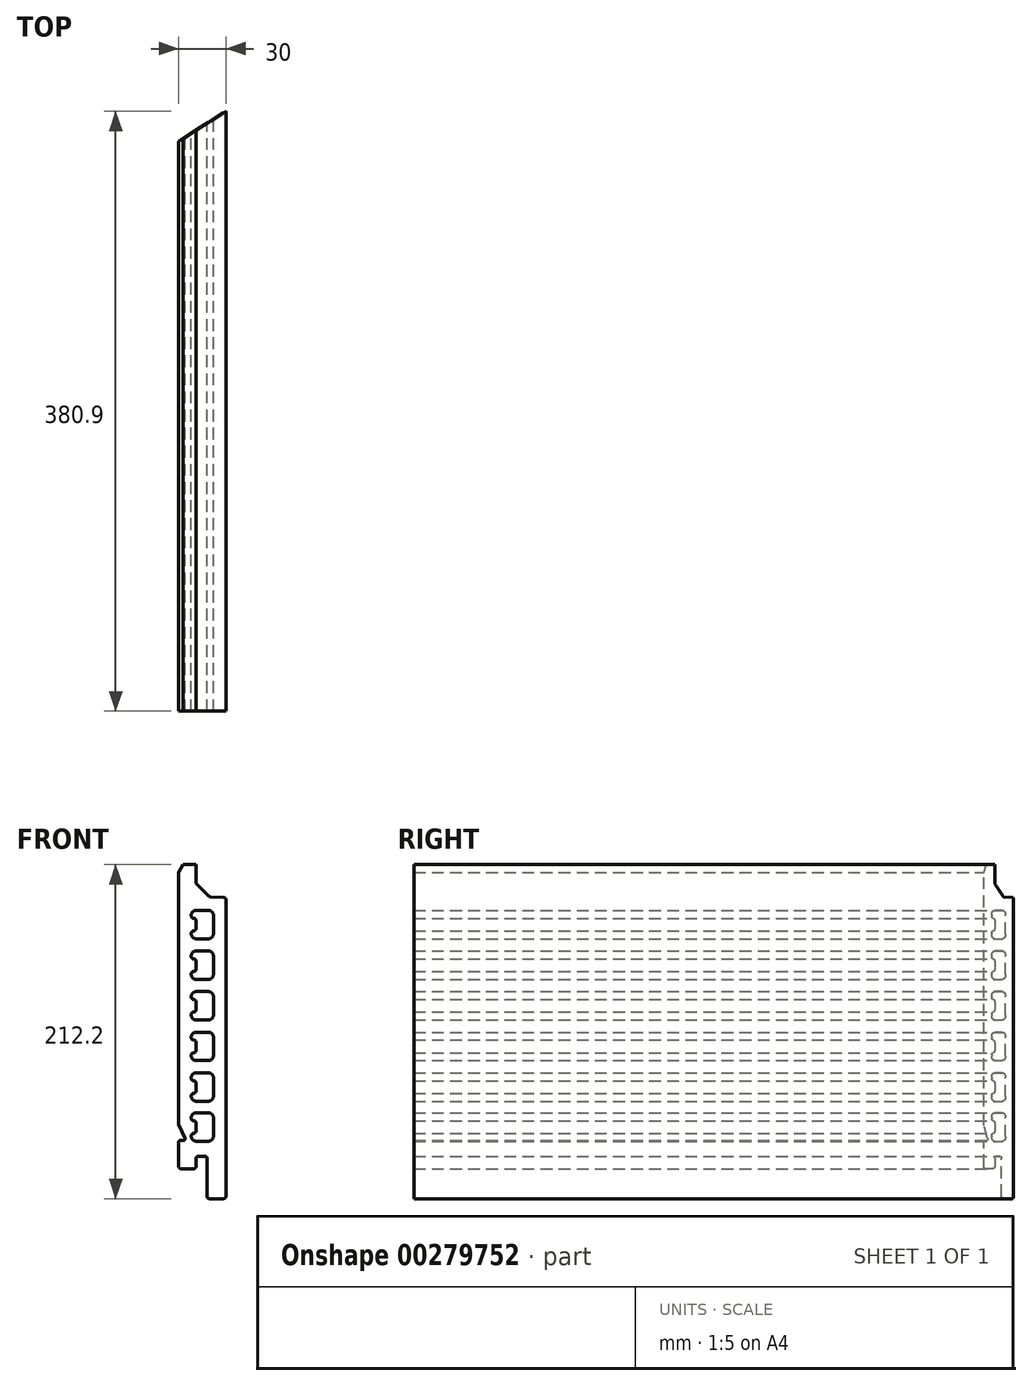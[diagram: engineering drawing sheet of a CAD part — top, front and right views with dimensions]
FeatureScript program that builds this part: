
annotation { "Feature Type Name" : "Feature", "Feature Type Description" : "" }
export const myFeature = defineFeature(function(context is Context, id is Id, definition is map)
    precondition{}
    {
        {
            var Q0;
            Q0=qCreatedBy(makeId("Front.planeOp"),FACE);
            var sketch = newSketch(context, id + "F0", { "sketchPlane" : qUnion([Q0])});
            skLineSegment(sketch, "E0", {"start": v(-14.86, -59.63) * mm, "end": v(-11.1, -67.7) * mm});
            skArc(sketch, "E1", {"start": v(-11.1, -67.7) * mm, "mid": v(-11.16, -68.66) * mm, "end": v(-12, -69.12) * mm});
            skLineSegment(sketch, "E2", {"start": v(-12, -69.12) * mm, "end": v(-14, -69.12) * mm});
            skArc(sketch, "E3", {"start": v(-14, -69.12) * mm, "mid": v(-14.7, -69.41) * mm, "end": v(-15, -70.12) * mm});
            skLineSegment(sketch, "E4", {"start": v(-15, -70.12) * mm, "end": v(-15, -85.6) * mm});
            skArc(sketch, "E5", {"start": v(-15, -85.6) * mm, "mid": v(-14.56, -86.66) * mm, "end": v(-13.5, -87.1) * mm});
            skLineSegment(sketch, "E6", {"start": v(-13.5, -87.1) * mm, "end": v(-5.5, -87.1) * mm});
            skArc(sketch, "E7", {"start": v(-5.5, -87.1) * mm, "mid": v(-4.44, -86.66) * mm, "end": v(-4, -85.6) * mm});
            skLineSegment(sketch, "E8", {"start": v(-4, -85.6) * mm, "end": v(-4, -80.6) * mm});
            skArc(sketch, "E9", {"start": v(-4, -80.6) * mm, "mid": v(-3.56, -79.54) * mm, "end": v(-2.5, -79.1) * mm});
            skLineSegment(sketch, "E10", {"start": v(-2.5, -79.1) * mm, "end": v(1.48, -79.1) * mm});
            skArc(sketch, "E11", {"start": v(1.48, -79.1) * mm, "mid": v(2.54, -79.54) * mm, "end": v(2.98, -80.6) * mm});
            skLineSegment(sketch, "E12", {"start": v(2.98, -80.6) * mm, "end": v(2.98, -104.6) * mm});
            skArc(sketch, "E13", {"start": v(2.98, -104.6) * mm, "mid": v(3.42, -105.66) * mm, "end": v(4.48, -106.1) * mm});
            skLineSegment(sketch, "E14", {"start": v(4.48, -106.1) * mm, "end": v(13.5, -106.1) * mm});
            skArc(sketch, "E15", {"start": v(13.5, -106.1) * mm, "mid": v(14.56, -105.66) * mm, "end": v(15, -104.6) * mm});
            skLineSegment(sketch, "E16", {"start": v(15, -104.6) * mm, "end": v(15, 83.78) * mm});
            skArc(sketch, "E17", {"start": v(15, 83.78) * mm, "mid": v(14.58, 84.81) * mm, "end": v(13.57, 85.27) * mm});
            skLineSegment(sketch, "E18", {"start": v(13.57, 85.27) * mm, "end": v(5.1, 85.66) * mm});
            skArc(sketch, "E19", {"start": v(5.1, 85.66) * mm, "mid": v(4.57, 85.79) * mm, "end": v(4.11, 86.1) * mm});
            skLineSegment(sketch, "E20", {"start": v(4.11, 86.1) * mm, "end": v(-3.56, 93.77) * mm});
            skArc(sketch, "E21", {"start": v(-3.56, 93.77) * mm, "mid": v(-3.89, 94.26) * mm, "end": v(-4, 94.83) * mm});
            skLineSegment(sketch, "E22", {"start": v(-4, 94.83) * mm, "end": v(-4, 106.1) * mm});
            skLineSegment(sketch, "E23", {"start": v(-4, 106.1) * mm, "end": v(-12.31, 106.1) * mm});
            skLineSegment(sketch, "E24", {"start": v(-12.31, 106.1) * mm, "end": v(-15, 101.2) * mm});
            skLineSegment(sketch, "E25", {"start": v(-15, 101.2) * mm, "end": v(-15, -59) * mm});
            skArc(sketch, "E26", {"start": v(-15, -59) * mm, "mid": v(-14.96, -59.32) * mm, "end": v(-14.86, -59.63) * mm});
            skArc(sketch, "E27", {"start": v(-14.86, -59.63) * mm, "mid": v(-14.96, -59.32) * mm, "end": v(-15, -59) * mm});
            skSolve(sketch);
        }
        {
            var Q0;
            Q0=makeQuery(id+"F0.imprint","IMPRINT",FACE,{"disambiguationData":[TD([[makeQuery(id+"F0.imprint","IMPRINT",EDGE,{"derivedFrom":sQuery(id+"F0.wireOp",EDGE,"E3")}),1.0]])]});
            extrude(context, id + "F1", {"entities" : qUnion([Q0]), "depth" : 381 * mm});
        }
        {
            var Q0;
            Q0=qCreatedBy(makeId("Front.planeOp"),FACE);
            var sketch = newSketch(context, id + "F2", { "sketchPlane" : qUnion([Q0])});
            skArc(sketch, "E28", {"start": v(-4, -32.7) * mm, "mid": v(-4.43, -31.63) * mm, "end": v(-5.5, -31.2) * mm});
            skLineSegment(sketch, "E29", {"start": v(-5.5, -31.2) * mm, "end": v(-5.5, -31.2) * mm});
            skArc(sketch, "E30", {"start": v(-5.5, -31.2) * mm, "mid": v(-6.56, -30.76) * mm, "end": v(-7, -29.7) * mm});
            skLineSegment(sketch, "E31", {"start": v(-7, -29.7) * mm, "end": v(-7, -29.2) * mm});
            skArc(sketch, "E32", {"start": v(-7, -29.2) * mm, "mid": v(-6.12, -27.07) * mm, "end": v(-4, -26.2) * mm});
            skLineSegment(sketch, "E33", {"start": v(-4, -26.2) * mm, "end": v(4, -26.2) * mm});
            skArc(sketch, "E34", {"start": v(4, -26.2) * mm, "mid": v(6.12, -27.07) * mm, "end": v(7, -29.2) * mm});
            skLineSegment(sketch, "E35", {"start": v(7, -29.2) * mm, "end": v(7, -41.2) * mm});
            skArc(sketch, "E36", {"start": v(7, -41.2) * mm, "mid": v(6.12, -43.32) * mm, "end": v(4, -44.2) * mm});
            skLineSegment(sketch, "E37", {"start": v(4, -44.2) * mm, "end": v(-4, -44.2) * mm});
            skArc(sketch, "E38", {"start": v(-4, -44.2) * mm, "mid": v(-6.12, -43.32) * mm, "end": v(-7, -41.2) * mm});
            skLineSegment(sketch, "E39", {"start": v(-7, -41.2) * mm, "end": v(-7, -40.7) * mm});
            skArc(sketch, "E40", {"start": v(-7, -40.7) * mm, "mid": v(-6.56, -39.63) * mm, "end": v(-5.5, -39.2) * mm});
            skLineSegment(sketch, "E41", {"start": v(-5.5, -39.2) * mm, "end": v(-5.5, -39.2) * mm});
            skArc(sketch, "E42", {"start": v(-5.5, -39.2) * mm, "mid": v(-4.43, -38.76) * mm, "end": v(-4, -37.7) * mm});
            skLineSegment(sketch, "E43", {"start": v(-4, -37.7) * mm, "end": v(-4, -32.7) * mm});
            skArc(sketch, "E44", {"start": v(-4, -58.1) * mm, "mid": v(-4.43, -57.03) * mm, "end": v(-5.5, -56.6) * mm});
            skLineSegment(sketch, "E45", {"start": v(-5.5, -56.6) * mm, "end": v(-5.5, -56.6) * mm});
            skArc(sketch, "E46", {"start": v(-5.5, -56.6) * mm, "mid": v(-6.56, -56.16) * mm, "end": v(-7, -55.1) * mm});
            skLineSegment(sketch, "E47", {"start": v(-7, -55.1) * mm, "end": v(-7, -54.6) * mm});
            skArc(sketch, "E48", {"start": v(-7, -54.6) * mm, "mid": v(-6.12, -52.47) * mm, "end": v(-4, -51.6) * mm});
            skLineSegment(sketch, "E49", {"start": v(-4, -51.6) * mm, "end": v(4, -51.6) * mm});
            skArc(sketch, "E50", {"start": v(4, -51.6) * mm, "mid": v(6.12, -52.47) * mm, "end": v(7, -54.6) * mm});
            skLineSegment(sketch, "E51", {"start": v(7, -54.6) * mm, "end": v(7, -66.6) * mm});
            skArc(sketch, "E52", {"start": v(7, -66.6) * mm, "mid": v(6.12, -68.72) * mm, "end": v(4, -69.6) * mm});
            skLineSegment(sketch, "E53", {"start": v(4, -69.6) * mm, "end": v(-4, -69.6) * mm});
            skArc(sketch, "E54", {"start": v(-4, -69.6) * mm, "mid": v(-6.12, -68.72) * mm, "end": v(-7, -66.6) * mm});
            skLineSegment(sketch, "E55", {"start": v(-7, -66.6) * mm, "end": v(-7, -66.1) * mm});
            skArc(sketch, "E56", {"start": v(-7, -66.1) * mm, "mid": v(-6.56, -65.03) * mm, "end": v(-5.5, -64.6) * mm});
            skLineSegment(sketch, "E57", {"start": v(-5.5, -64.6) * mm, "end": v(-5.5, -64.6) * mm});
            skArc(sketch, "E58", {"start": v(-5.5, -64.6) * mm, "mid": v(-4.43, -64.16) * mm, "end": v(-4, -63.1) * mm});
            skLineSegment(sketch, "E59", {"start": v(-4, -63.1) * mm, "end": v(-4, -58.1) * mm});
            skArc(sketch, "E60", {"start": v(-4, -6.9) * mm, "mid": v(-4.43, -5.83) * mm, "end": v(-5.5, -5.4) * mm});
            skLineSegment(sketch, "E61", {"start": v(-5.5, -5.4) * mm, "end": v(-5.5, -5.4) * mm});
            skArc(sketch, "E62", {"start": v(-5.5, -5.4) * mm, "mid": v(-6.56, -4.96) * mm, "end": v(-7, -3.9) * mm});
            skLineSegment(sketch, "E63", {"start": v(-7, -3.9) * mm, "end": v(-7, -3.4) * mm});
            skArc(sketch, "E64", {"start": v(-7, -3.4) * mm, "mid": v(-6.12, -1.27) * mm, "end": v(-4, -0.4) * mm});
            skLineSegment(sketch, "E65", {"start": v(-4, -0.4) * mm, "end": v(4, -0.4) * mm});
            skArc(sketch, "E66", {"start": v(4, -0.4) * mm, "mid": v(6.12, -1.27) * mm, "end": v(7, -3.4) * mm});
            skLineSegment(sketch, "E67", {"start": v(7, -3.4) * mm, "end": v(7, -15.4) * mm});
            skArc(sketch, "E68", {"start": v(7, -15.4) * mm, "mid": v(6.12, -17.52) * mm, "end": v(4, -18.4) * mm});
            skLineSegment(sketch, "E69", {"start": v(4, -18.4) * mm, "end": v(-4, -18.4) * mm});
            skArc(sketch, "E70", {"start": v(-4, -18.4) * mm, "mid": v(-6.12, -17.52) * mm, "end": v(-7, -15.4) * mm});
            skLineSegment(sketch, "E71", {"start": v(-7, -15.4) * mm, "end": v(-7, -14.9) * mm});
            skArc(sketch, "E72", {"start": v(-7, -14.9) * mm, "mid": v(-6.56, -13.83) * mm, "end": v(-5.5, -13.4) * mm});
            skLineSegment(sketch, "E73", {"start": v(-5.5, -13.4) * mm, "end": v(-5.5, -13.4) * mm});
            skArc(sketch, "E74", {"start": v(-5.5, -13.4) * mm, "mid": v(-4.43, -12.96) * mm, "end": v(-4, -11.9) * mm});
            skLineSegment(sketch, "E75", {"start": v(-4, -11.9) * mm, "end": v(-4, -6.9) * mm});
            skLineSegment(sketch, "E76", {"start": v(-5.5, 20.4) * mm, "end": v(-5.5, 20.4) * mm});
            skArc(sketch, "E77", {"start": v(-5.5, 20.4) * mm, "mid": v(-6.56, 20.84) * mm, "end": v(-7, 21.9) * mm});
            skLineSegment(sketch, "E78", {"start": v(-7, 21.9) * mm, "end": v(-7, 22.4) * mm});
            skArc(sketch, "E79", {"start": v(-7, 22.4) * mm, "mid": v(-6.12, 24.52) * mm, "end": v(-4, 25.4) * mm});
            skLineSegment(sketch, "E80", {"start": v(-4, 25.4) * mm, "end": v(4, 25.4) * mm});
            skArc(sketch, "E81", {"start": v(4, 25.4) * mm, "mid": v(6.12, 24.52) * mm, "end": v(7, 22.4) * mm});
            skLineSegment(sketch, "E82", {"start": v(7, 22.4) * mm, "end": v(7, 10.4) * mm});
            skArc(sketch, "E83", {"start": v(7, 10.4) * mm, "mid": v(6.12, 8.28) * mm, "end": v(4, 7.4) * mm});
            skLineSegment(sketch, "E84", {"start": v(4, 7.4) * mm, "end": v(-4, 7.4) * mm});
            skArc(sketch, "E85", {"start": v(-4, 7.4) * mm, "mid": v(-6.12, 8.28) * mm, "end": v(-7, 10.4) * mm});
            skLineSegment(sketch, "E86", {"start": v(-7, 10.4) * mm, "end": v(-7, 10.9) * mm});
            skArc(sketch, "E87", {"start": v(-7, 10.9) * mm, "mid": v(-6.56, 11.96) * mm, "end": v(-5.5, 12.4) * mm});
            skLineSegment(sketch, "E88", {"start": v(-5.5, 12.4) * mm, "end": v(-5.5, 12.4) * mm});
            skArc(sketch, "E89", {"start": v(-5.5, 12.4) * mm, "mid": v(-4.43, 12.84) * mm, "end": v(-4, 13.9) * mm});
            skLineSegment(sketch, "E90", {"start": v(-4, 13.9) * mm, "end": v(-4, 18.9) * mm});
            skArc(sketch, "E91", {"start": v(-4, 18.9) * mm, "mid": v(-4.43, 19.96) * mm, "end": v(-5.5, 20.4) * mm});
            skLineSegment(sketch, "E92", {"start": v(-5.5, 46.2) * mm, "end": v(-5.5, 46.2) * mm});
            skArc(sketch, "E93", {"start": v(-5.5, 46.2) * mm, "mid": v(-6.56, 46.64) * mm, "end": v(-7, 47.7) * mm});
            skLineSegment(sketch, "E94", {"start": v(-7, 47.7) * mm, "end": v(-7, 48.2) * mm});
            skArc(sketch, "E95", {"start": v(-7, 48.2) * mm, "mid": v(-6.12, 50.32) * mm, "end": v(-4, 51.2) * mm});
            skLineSegment(sketch, "E96", {"start": v(-4, 51.2) * mm, "end": v(4, 51.2) * mm});
            skArc(sketch, "E97", {"start": v(4, 51.2) * mm, "mid": v(6.12, 50.32) * mm, "end": v(7, 48.2) * mm});
            skLineSegment(sketch, "E98", {"start": v(7, 48.2) * mm, "end": v(7, 36.2) * mm});
            skArc(sketch, "E99", {"start": v(7, 36.2) * mm, "mid": v(6.12, 34.08) * mm, "end": v(4, 33.2) * mm});
            skLineSegment(sketch, "E100", {"start": v(4, 33.2) * mm, "end": v(-4, 33.2) * mm});
            skArc(sketch, "E101", {"start": v(-4, 33.2) * mm, "mid": v(-6.12, 34.08) * mm, "end": v(-7, 36.2) * mm});
            skLineSegment(sketch, "E102", {"start": v(-7, 36.2) * mm, "end": v(-7, 36.7) * mm});
            skArc(sketch, "E103", {"start": v(-7, 36.7) * mm, "mid": v(-6.56, 37.76) * mm, "end": v(-5.5, 38.2) * mm});
            skLineSegment(sketch, "E104", {"start": v(-5.5, 38.2) * mm, "end": v(-5.5, 38.2) * mm});
            skArc(sketch, "E105", {"start": v(-5.5, 38.2) * mm, "mid": v(-4.43, 38.64) * mm, "end": v(-4, 39.7) * mm});
            skLineSegment(sketch, "E106", {"start": v(-4, 39.7) * mm, "end": v(-4, 44.7) * mm});
            skArc(sketch, "E107", {"start": v(-4, 44.7) * mm, "mid": v(-4.43, 45.76) * mm, "end": v(-5.5, 46.2) * mm});
            skLineSegment(sketch, "E108", {"start": v(-5.5, 72) * mm, "end": v(-5.5, 72) * mm});
            skArc(sketch, "E109", {"start": v(-5.5, 72) * mm, "mid": v(-6.56, 72.43) * mm, "end": v(-7, 73.5) * mm});
            skLineSegment(sketch, "E110", {"start": v(-7, 73.5) * mm, "end": v(-7, 74) * mm});
            skArc(sketch, "E111", {"start": v(-7, 74) * mm, "mid": v(-6.12, 76.12) * mm, "end": v(-4, 77) * mm});
            skLineSegment(sketch, "E112", {"start": v(-4, 77) * mm, "end": v(4, 77) * mm});
            skArc(sketch, "E113", {"start": v(4, 77) * mm, "mid": v(6.12, 76.12) * mm, "end": v(7, 74) * mm});
            skLineSegment(sketch, "E114", {"start": v(7, 74) * mm, "end": v(7, 62) * mm});
            skArc(sketch, "E115", {"start": v(7, 62) * mm, "mid": v(6.12, 59.87) * mm, "end": v(4, 59) * mm});
            skLineSegment(sketch, "E116", {"start": v(4, 59) * mm, "end": v(-4, 59) * mm});
            skArc(sketch, "E117", {"start": v(-4, 59) * mm, "mid": v(-6.12, 59.87) * mm, "end": v(-7, 62) * mm});
            skLineSegment(sketch, "E118", {"start": v(-7, 62) * mm, "end": v(-7, 62.5) * mm});
            skArc(sketch, "E119", {"start": v(-7, 62.5) * mm, "mid": v(-6.56, 63.56) * mm, "end": v(-5.5, 64) * mm});
            skLineSegment(sketch, "E120", {"start": v(-5.5, 64) * mm, "end": v(-5.5, 64) * mm});
            skArc(sketch, "E121", {"start": v(-5.5, 64) * mm, "mid": v(-4.43, 64.43) * mm, "end": v(-4, 65.5) * mm});
            skLineSegment(sketch, "E122", {"start": v(-4, 65.5) * mm, "end": v(-4, 70.5) * mm});
            skArc(sketch, "E123", {"start": v(-4, 70.5) * mm, "mid": v(-4.43, 71.56) * mm, "end": v(-5.5, 72) * mm});
            skLineSegment(sketch, "E124", {"start": v(0, -69.6) * mm, "end": v(-0.5, -77) * mm});
            skSolve(sketch);
        }
        {
            var Q0;
            Q0=qSketchRegion(id+"F2",true);
            extrude(context, id + "F3", {"entities" : qUnion([Q0]), "operationType" : NewBodyOperationType.REMOVE, "depth" : 711.2 * mm});
        }
        {
            var Q0;
            Q0=qCreatedBy(makeId("Top.planeOp"),FACE);
            var sketch = newSketch(context, id + "F4", { "sketchPlane" : qUnion([Q0])});
            skLineSegment(sketch, "E125", {"start": v(-15.1, 0) * mm, "end": v(15.16, 0) * mm});
            skLineSegment(sketch, "E126", {"start": v(15.16, 0) * mm, "end": v(-15.1, -19.05) * mm});
            skLineSegment(sketch, "E127", {"start": v(-15.1, -19.05) * mm, "end": v(-15.1, 0) * mm});
            skSolve(sketch);
        }
        {
            var Q0;
            Q0 = qSketchRegion(id + "F4", true);
            extrude(context, id + "F5", {"entities" : qUnion([Q0]), "operationType" : NewBodyOperationType.REMOVE, "endBound" : BoundingType.THROUGH_ALL, "oppositeDirection" : true, "depth" : 25.4 * mm, "hasSecondDirection" : true, "secondDirectionBound" : SecondDirectionBoundingType.THROUGH_ALL, "secondDirectionOppositeDirection" : false, "secondDirectionDepth" : 25.4 * mm});
        }
    });
